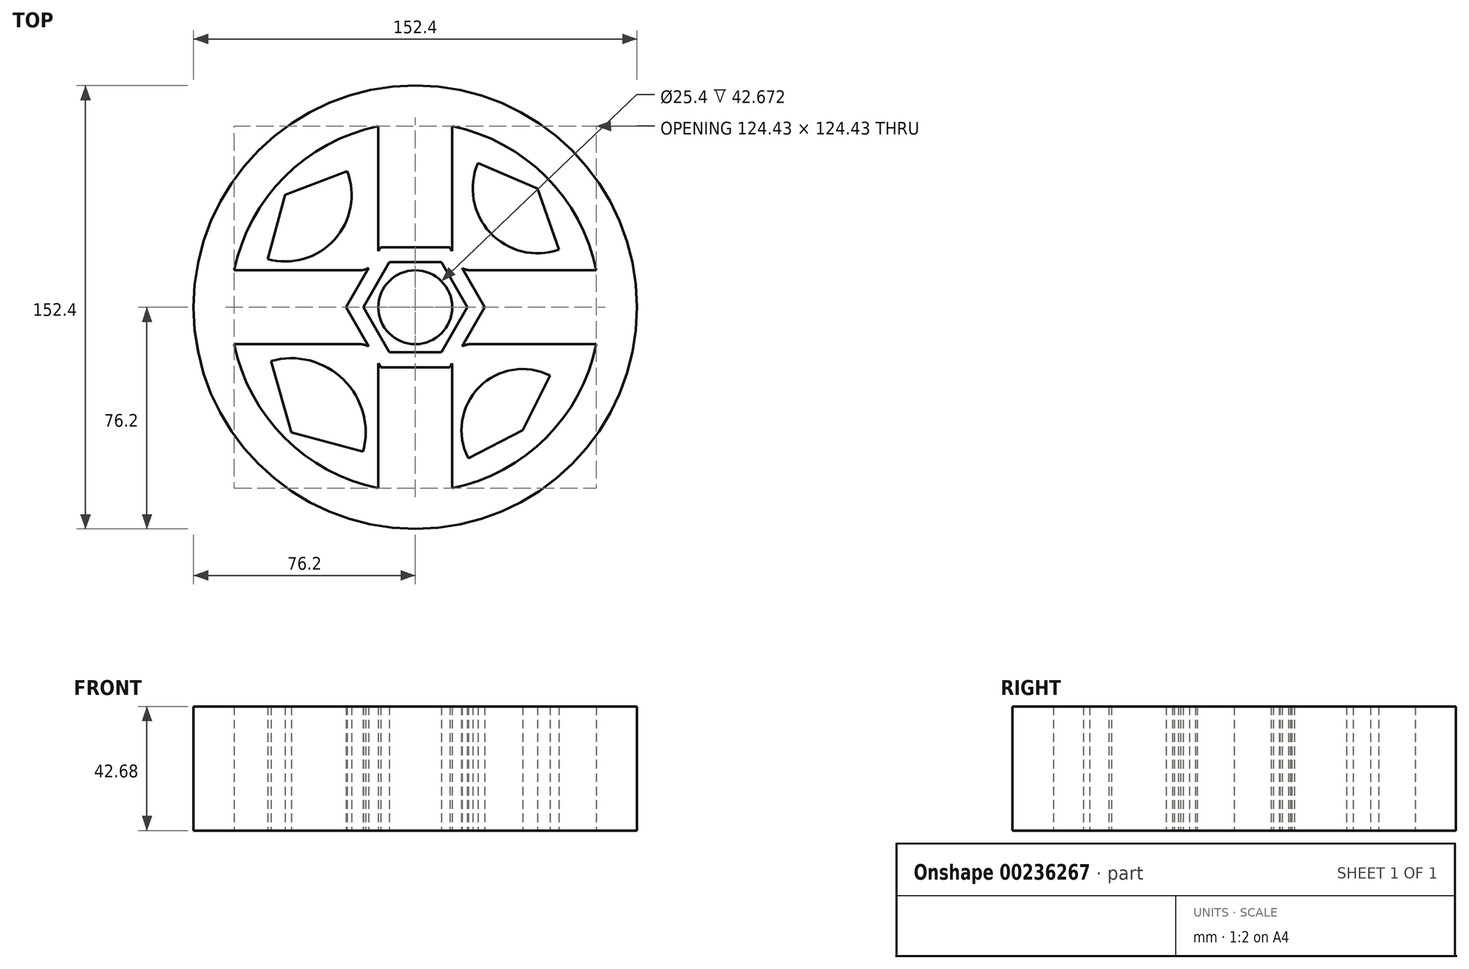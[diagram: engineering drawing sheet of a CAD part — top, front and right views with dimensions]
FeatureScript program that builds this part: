
annotation { "Feature Type Name" : "Feature", "Feature Type Description" : "" }
export const myFeature = defineFeature(function(context is Context, id is Id, definition is map)
    precondition{}
    {
        {
            var Q0;
            Q0=qCreatedBy(makeId("Top.planeOp"),FACE);
            var sketch = newSketch(context, id + "F0", { "sketchPlane" : qUnion([Q0])});
            skCircle(sketch, "E0", {"center": v(0, 0) * mm, "radius": 76.2 * mm});
            skArc(sketch, "E1", {"start": v(12.7, -62.22) * mm, "mid": v(44.9, -44.9) * mm, "end": v(62.22, -12.7) * mm});
            skCircle(sketch, "E2", {"center": v(0, 0) * mm, "radius": 12.7 * mm});
            skLineSegment(sketch, "E3", {"start": v(0, 0) * mm, "end": v(0, 12.7) * mm});
            skLineSegment(sketch, "E4.0", {"start": v(12.7, 19.05) * mm, "end": v(12.7, 62.22) * mm});
            skLineSegment(sketch, "E5.0", {"start": v(-12.7, 19.05) * mm, "end": v(-12.7, 62.22) * mm});
            skLineSegment(sketch, "E6", {"start": v(-63.5, 0) * mm, "end": v(63.5, 0) * mm});
            skLineSegment(sketch, "E7.0", {"start": v(-76.2, 12.7) * mm, "end": v(-75.13, 12.7) * mm});
            skLineSegment(sketch, "E8.0", {"start": v(-76.2, -12.7) * mm, "end": v(-75.13, -12.7) * mm});
            skLineSegment(sketch, "E9", {"start": v(0, 0) * mm, "end": v(0, -63.5) * mm});
            skPoint(sketch, "E9.endSnap0", {"position": v(0, -12.7) * mm});
            skLineSegment(sketch, "E10.0", {"start": v(-12.7, -19.05) * mm, "end": v(-12.7, -62.22) * mm});
            skLineSegment(sketch, "E11.0", {"start": v(12.7, -19.05) * mm, "end": v(12.7, -62.22) * mm});
            skLineSegment(sketch, "E12.trimOffspring", {"start": v(-12.7, -75.13) * mm, "end": v(-12.7, -76.2) * mm});
            skPoint(sketch, "E13.orphan", {"position": v(0, -76.2) * mm});
            skLineSegment(sketch, "E14.trimOffspring", {"start": v(12.7, -75.13) * mm, "end": v(12.7, -76.2) * mm});
            skLineSegment(sketch, "E15.trimOffspring", {"start": v(75.13, -12.7) * mm, "end": v(76.2, -12.7) * mm});
            skLineSegment(sketch, "E16.trimOffspring", {"start": v(75.13, 12.7) * mm, "end": v(76.2, 12.7) * mm});
            skLineSegment(sketch, "E17.trimOffspring", {"start": v(12.7, 75.13) * mm, "end": v(12.7, 76.2) * mm});
            skLineSegment(sketch, "E18.trimOffspring", {"start": v(-12.7, 75.13) * mm, "end": v(-12.7, 76.2) * mm});
            skLineSegment(sketch, "E19.trimOffspring", {"start": v(-62.22, 12.7) * mm, "end": v(-19.05, 12.7) * mm});
            skPoint(sketch, "E20.orphan", {"position": v(-76.2, 0) * mm});
            skLineSegment(sketch, "E21.trimOffspring", {"start": v(-62.22, -12.7) * mm, "end": v(-19.05, -12.7) * mm});
            skLineSegment(sketch, "E22.trimOffspring", {"start": v(19.05, 12.7) * mm, "end": v(62.22, 12.7) * mm});
            skLineSegment(sketch, "E23.trimOffspring", {"start": v(19.05, -12.7) * mm, "end": v(62.22, -12.7) * mm});
            skLineSegment(sketch, "E24.0", {"start": v(-63.5, -127) * mm, "end": v(63.5, -127) * mm});
            skArc(sketch, "E25.trimOffspring", {"start": v(62.22, 12.7) * mm, "mid": v(44.9, 44.9) * mm, "end": v(12.7, 62.22) * mm});
            skArc(sketch, "E26.trimOffspring", {"start": v(-12.7, 62.22) * mm, "mid": v(-44.9, 44.9) * mm, "end": v(-62.22, 12.7) * mm});
            skArc(sketch, "E27.trimOffspring", {"start": v(-62.22, -12.7) * mm, "mid": v(-44.9, -44.9) * mm, "end": v(-12.7, -62.22) * mm});
            skPoint(sketch, "E28.visualSharp", {"position": v(-12.7, 12.7) * mm});
            skArc(sketch, "E28.filletArc", {"start": v(-19.05, 12.7) * mm, "mid": v(-14.56, 14.56) * mm, "end": v(-12.7, 19.05) * mm});
            skPoint(sketch, "E29.visualSharp", {"position": v(12.7, 12.7) * mm});
            skArc(sketch, "E29.filletArc", {"start": v(12.7, 19.05) * mm, "mid": v(14.56, 14.56) * mm, "end": v(19.05, 12.7) * mm});
            skPoint(sketch, "E30.visualSharp", {"position": v(12.7, -12.7) * mm});
            skArc(sketch, "E30.filletArc", {"start": v(19.05, -12.7) * mm, "mid": v(14.56, -14.56) * mm, "end": v(12.7, -19.05) * mm});
            skPoint(sketch, "E31.visualSharp", {"position": v(-12.7, -12.7) * mm});
            skArc(sketch, "E31.filletArc", {"start": v(-12.7, -19.05) * mm, "mid": v(-14.56, -14.56) * mm, "end": v(-19.05, -12.7) * mm});
            skCircle(sketch, "E32.cCircle", {"center": v(0, 0) * mm, "radius": 15.48 * mm, "construction": true});
            skLineSegment(sketch, "E32.0", {"start": v(8.94, -15.48) * mm, "end": v(-8.94, -15.48) * mm});
            skLineSegment(sketch, "E32.1", {"start": v(-8.94, -15.48) * mm, "end": v(-17.87, 0) * mm});
            skLineSegment(sketch, "E32.2", {"start": v(-17.87, 0) * mm, "end": v(-8.94, 15.48) * mm});
            skLineSegment(sketch, "E32.3", {"start": v(-8.94, 15.48) * mm, "end": v(8.94, 15.48) * mm});
            skLineSegment(sketch, "E32.4", {"start": v(8.94, 15.48) * mm, "end": v(17.87, 0) * mm});
            skLineSegment(sketch, "E32.5", {"start": v(17.87, 0) * mm, "end": v(8.94, -15.48) * mm});
            skPoint(sketch, "E32.0.midPoint", {"position": v(0, -15.48) * mm});
            skCircle(sketch, "E33.cCircle", {"center": v(0, 0) * mm, "radius": 20.64 * mm, "construction": true});
            skLineSegment(sketch, "E33.0", {"start": v(-11.91, -20.64) * mm, "end": v(-23.83, 0) * mm});
            skLineSegment(sketch, "E33.1", {"start": v(-23.83, 0) * mm, "end": v(-11.91, 20.64) * mm});
            skLineSegment(sketch, "E33.2", {"start": v(-11.91, 20.64) * mm, "end": v(11.91, 20.64) * mm});
            skLineSegment(sketch, "E33.3", {"start": v(11.91, 20.64) * mm, "end": v(23.83, 0) * mm});
            skLineSegment(sketch, "E33.4", {"start": v(23.83, 0) * mm, "end": v(11.91, -20.64) * mm});
            skLineSegment(sketch, "E33.5", {"start": v(11.91, -20.64) * mm, "end": v(-11.91, -20.64) * mm});
            skPoint(sketch, "E33.0.midPoint", {"position": v(-17.87, -10.32) * mm});
            skArc(sketch, "E34", {"start": v(-17.92, -49.66) * mm, "mid": v(-24.7, -24.85) * mm, "end": v(-49.62, -18.5) * mm});
            skArc(sketch, "E35", {"start": v(46.31, -23.47) * mm, "mid": v(21.95, -27.47) * mm, "end": v(18.2, -51.86) * mm});
            skArc(sketch, "E36", {"start": v(21.5, 49.58) * mm, "mid": v(25.72, 25.62) * mm, "end": v(49.34, 19.8) * mm});
            skArc(sketch, "E37", {"start": v(-50.72, 16.5) * mm, "mid": v(-27.76, 23.28) * mm, "end": v(-23.43, 46.82) * mm});
            skLineSegment(sketch, "E38", {"start": v(21.5, 49.58) * mm, "end": v(42, 40.84) * mm});
            skLineSegment(sketch, "E39", {"start": v(42, 40.84) * mm, "end": v(49.34, 19.8) * mm});
            skLineSegment(sketch, "E40", {"start": v(36.89, -42.26) * mm, "end": v(46.31, -23.47) * mm});
            skLineSegment(sketch, "E41", {"start": v(36.89, -42.26) * mm, "end": v(18.2, -51.86) * mm});
            skLineSegment(sketch, "E42", {"start": v(-17.92, -49.66) * mm, "end": v(-42.6, -43.08) * mm});
            skLineSegment(sketch, "E43", {"start": v(-42.6, -43.08) * mm, "end": v(-49.62, -18.5) * mm});
            skLineSegment(sketch, "E44", {"start": v(-50.72, 16.5) * mm, "end": v(-44.76, 38.58) * mm});
            skLineSegment(sketch, "E45", {"start": v(-23.43, 46.82) * mm, "end": v(-44.76, 38.58) * mm});
            skSolve(sketch);
        }
        {
            var Q0;
            Q0 = qSketchRegion(id + "F0", true);
            var Q1;
            {var subQ0=sQuery(id+"F0.wireOp",EDGE,"E32.5");Q1=makeQuery(id+"F0.imprint","IMPRINT",FACE,{"disambiguationData":[TD([[makeQuery(id+"F0.imprint","IMPRINT",EDGE,{"derivedFrom":subQ0}),-1.0]])]});}
            var Q2;
            {var subQ5=sQuery(id+"F0.wireOp",EDGE,"E32.2");Q2=makeQuery(id+"F0.imprint","IMPRINT",FACE,{"disambiguationData":[TD([[makeQuery(id+"F0.imprint","IMPRINT",EDGE,{"derivedFrom":subQ5}),-1.0]])]});}
            var Q3;
            {var subQ0=sQuery(id+"F0.wireOp",EDGE,"E32.1");Q3=makeQuery(id+"F0.imprint","IMPRINT",FACE,{"disambiguationData":[TD([[makeQuery(id+"F0.imprint","IMPRINT",EDGE,{"derivedFrom":subQ0}),-1.0]])]});}
            var Q4;
            Q4=makeQuery(id+"F0.imprint","IMPRINT",FACE,{"disambiguationData":[TD([[makeQuery(id+"F0.imprint","IMPRINT",EDGE,{"derivedFrom":sQuery(id+"F0.wireOp",EDGE,"E34")}),1.0]])]});
            var Q5;
            Q5=makeQuery(id+"F0.imprint","IMPRINT",FACE,{"disambiguationData":[TD([[makeQuery(id+"F0.imprint","IMPRINT",EDGE,{"derivedFrom":sQuery(id+"F0.wireOp",EDGE,"E35")}),1.0]])]});
            var Q6;
            Q6=makeQuery(id+"F0.imprint","IMPRINT",FACE,{"disambiguationData":[TD([[makeQuery(id+"F0.imprint","IMPRINT",EDGE,{"derivedFrom":sQuery(id+"F0.wireOp",EDGE,"E36")}),1.0]])]});
            var Q7;
            Q7=makeQuery(id+"F0.imprint","IMPRINT",FACE,{"disambiguationData":[TD([[makeQuery(id+"F0.imprint","IMPRINT",EDGE,{"derivedFrom":sQuery(id+"F0.wireOp",EDGE,"E37")}),1.0]])]});
            extrude(context, id + "F1", {"entities" : qUnion([Q0, Q1, Q2, Q3, Q4, Q5, Q6, Q7]), "endBound" : BoundingType.SYMMETRIC, "depth" : 42.67 * mm});
        }
    });
